# Revit family: Fam Bticino door entry system IP standard indoor unit
name_source: partatom
category: Tableaux/Baies
units: mm (PartAtom-declared; Revit-internal decimal feet)

## family parameters
Configuration du panneau = Deux colonnes, circuits au sein
Conserver l'orientation des annotations = Non
Cote de connecteur circulaire = Utiliser le diamètre
Couper avec des vides une fois chargée = Non
Hôte = Face
Partagée = Non
Repère de localisation dans la pièce = Non
Type d'élément = Tableau de raccordement

## types (4) — shared parameters
Connection type = RJ45 cable
Elévation par défaut = 1500 mm  [stored 4.92126 ft]
Etim class = LC000779 Indoor station door communication
Fabricant = BTICINO
General terms of use = https://assets.legrand.com
Height = 122 mm  [stored 0.400262 ft]
IP = 30
Installation method = Surface
Interface type = Wire network
Operating temperature min max = -10/+40 °C
Photo = https://assets.legrand.com
Touch screen = Oui
Width = 189 mm  [stored 0.620079 ft]
With camera = Non

## per-type parameters (varying)
| type | Color | Contour champagne | Contour miroir | EAN | Plaque champagne | Plaque miroir | Plaque noire | Product designation | Reference | Tension |
| Standard type black 24V | Black | Non | Oui | 8005543710722 | Non | Non | Oui | BTicino  door entry system IP standard indoor unit black BT-373005 | BT-373005 | 24 V DC |
| Standard type champagne | Champagne | Oui | Non | 8005543710746 | Oui | Non | Non | BTicino  door entry system IP standard indoor unit champagne BT-373006 | BT-373006 | 24 V DC |
| Standard type mirror | Mirror | Oui | Non | 8005543710760 | Non | Oui | Non | BTicino  door entry system IP standard indoor unit mirror BT-373007 | BT-373007 | 24 V DC |
| Standard type black 48V | Black | Non | Oui | 8005543744451 | Non | Non | Oui | BTicino door entry system IP standard indoor unit black BT-373008 | BT-373008 | 48 V DC |

note: [stored X ft] marks values corroborated as IEEE doubles in the binary element streams (Revit-internal decimal feet)
